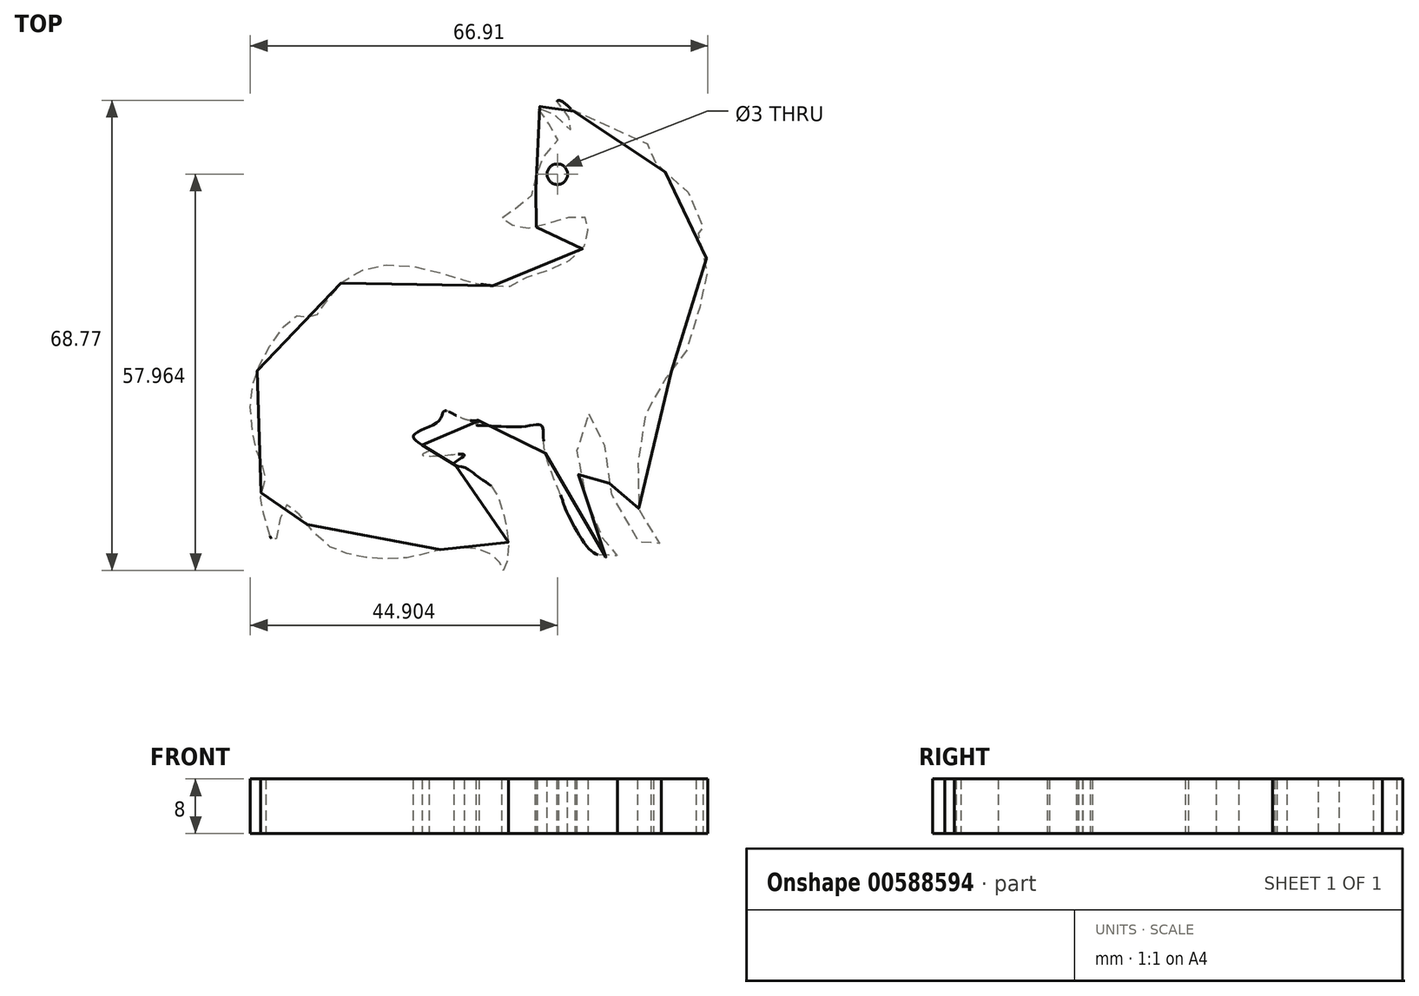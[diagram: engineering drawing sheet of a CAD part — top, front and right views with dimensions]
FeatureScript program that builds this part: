
annotation { "Feature Type Name" : "Feature", "Feature Type Description" : "" }
export const myFeature = defineFeature(function(context is Context, id is Id, definition is map)
    precondition{}
    {
        {
            var Q0;
            Q0=qCreatedBy(makeId("Top.planeOp"),FACE);
            var sketch = newSketch(context, id + "F0", { "sketchPlane" : qUnion([Q0])});
            skFitSpline(sketch, "E0", {"points": [v(-34.25, 47.86) * mm, v(-31.91, 47.77) * mm, v(-29.28, 49.14) * mm, v(-25.7, 50.3) * mm, v(-21.87, 52.47) * mm, v(-20.48, 54.69) * mm, v(-20.36, 56.67) * mm, v(-20.64, 57.8) * mm, v(-22.78, 57.95) * mm, v(-25.47, 57.17) * mm, v(-29.23, 56.24) * mm, v(-31.22, 56.6) * mm, v(-33, 57.6) * mm, v(-32.34, 58.24) * mm, v(-29.98, 59.93) * mm, v(-27.93, 62.25) * mm, v(-27.97, 65.04) * mm, v(-24.87, 68.94) * mm, v(-25.35, 70.78) * mm, v(-27.77, 73.83) * mm, v(-26.33, 73.83) * mm, v(-23.01, 70.69) * mm, v(-22.3, 71.31) * mm, v(-24.9, 74.46) * mm, v(-24.54, 75) * mm, v(-20.95, 72.12) * mm, v(-18.7, 71.94) * mm, v(-10.8, 67.72) * mm, v(-11.16, 67) * mm, v(-7.66, 63.32) * mm, v(-4.16, 59.1) * mm, v(-3.71, 55.96) * mm, v(-4.52, 56.6) * mm, v(-2.9, 51.3) * mm, v(-3.26, 48.87) * mm, v(-4.34, 43.04) * mm, v(-6.76, 37.02) * mm, v(-9.37, 33.88) * mm, v(-12.3, 27.84) * mm, v(-13.11, 19.23) * mm, v(-11.94, 12.5) * mm, v(-9.63, 9.59) * mm, v(-12.73, 10.26) * mm, v(-17.43, 19.8) * mm, v(-18.38, 26.67) * mm, v(-20.66, 29.22) * mm, v(-21.87, 21.15) * mm, v(-19.73, 14.57) * mm, v(-17.27, 9.55) * mm, v(-16.07, 8.7) * mm, v(-16.37, 8.1) * mm, v(-17.8, 8.18) * mm, v(-20.14, 9.33) * mm, v(-23.9, 15.85) * mm, v(-24.16, 16.7) * mm, v(-26.75, 24.15) * mm, v(-27.17, 27.42) * mm, v(-29.75, 27.29) * mm, v(-36.24, 27.46) * mm, v(-36.75, 27.54) * mm, v(-36.28, 28.1) * mm, v(-37.97, 28.22) * mm, v(-41.32, 29.58) * mm, v(-42.17, 28.14) * mm, v(-45.9, 25.98) * mm, v(-44.63, 24.58) * mm, v(-43.65, 23.73) * mm, v(-44.58, 23.18) * mm, v(-42.68, 22.97) * mm, v(-38.57, 23.22) * mm, v(-38.48, 23.01) * mm, v(-40, 21.82) * mm, v(-38.31, 21.23) * mm, v(-36.28, 19.8) * mm, v(-34.16, 18.18) * mm, v(-32.64, 14.11) * mm, v(-32, 9.11) * mm, v(-32.68, 6.23) * mm, v(-33.27, 7.38) * mm, v(-35.43, 9.03) * mm, v(-40.6, 9.54) * mm, v(-46.66, 8.1) * mm, v(-54.33, 8.4) * mm, v(-60.05, 11.32) * mm, v(-64.67, 15.68) * mm, v(-66.18, 10.34) * mm, v(-68.1, 15.78) * mm, v(-68.1, 17.8) * mm, v(-67.5, 19.81) * mm, v(-68.5, 22.84) * mm, v(-69.71, 31.1) * mm, v(-67.2, 38.56) * mm, v(-62.56, 43.6) * mm, v(-60.64, 43.2) * mm, v(-57.12, 47.62) * mm, v(-48.15, 50.95) * mm, v(-37.16, 48.33) * mm, v(-34.25, 47.86) * mm]});
            skSolve(sketch);
        }
        {
            var Q0;
            Q0 = qSketchRegion(id + "F0", true);
            extrude(context, id + "F1", {"entities" : qUnion([Q0]), "depth" : 8 * mm, "offsetDistance" : 25 * mm});
        }
        {
            var Q0;
            Q0=makeQuery(id+"F1.opExtrude","CAP_FACE",FACE,{"disambiguationData":[OSD([sQuery(id+"F0.wireOp",EDGE,"E0")])],"isStart":false});
            var sketch = newSketch(context, id + "F2", { "sketchPlane" : qUnion([Q0])});
            skPoint(sketch, "E1", {"position": v(-24.84, 64.2) * mm});
            skSolve(sketch);
        }
        {
            var Q0;
            Q0=sQuery(id+"F2.wireOp",VERTEX,"E1");
            var Q1;
            Q1=makeQuery(id+"F1.opExtrude","SWEPT_BODY",BODY,{"disambiguationData":[OSD([sQuery(id+"F0.wireOp",EDGE,"E0")])]});
            hole(context, id + "F3", {"style" : HoleStyle.SIMPLE, "endStyle" : HoleEndStyle.THROUGH, "holeDiameter" : 3 * mm, "majorDiameter" : 5 * mm, "isTappedThrough" : true, "tappedDepth" : 12 * mm, "tapClearance" : 3, "locations" : qUnion([Q0]), "scope" : qUnion([Q1])});
        }
    });
